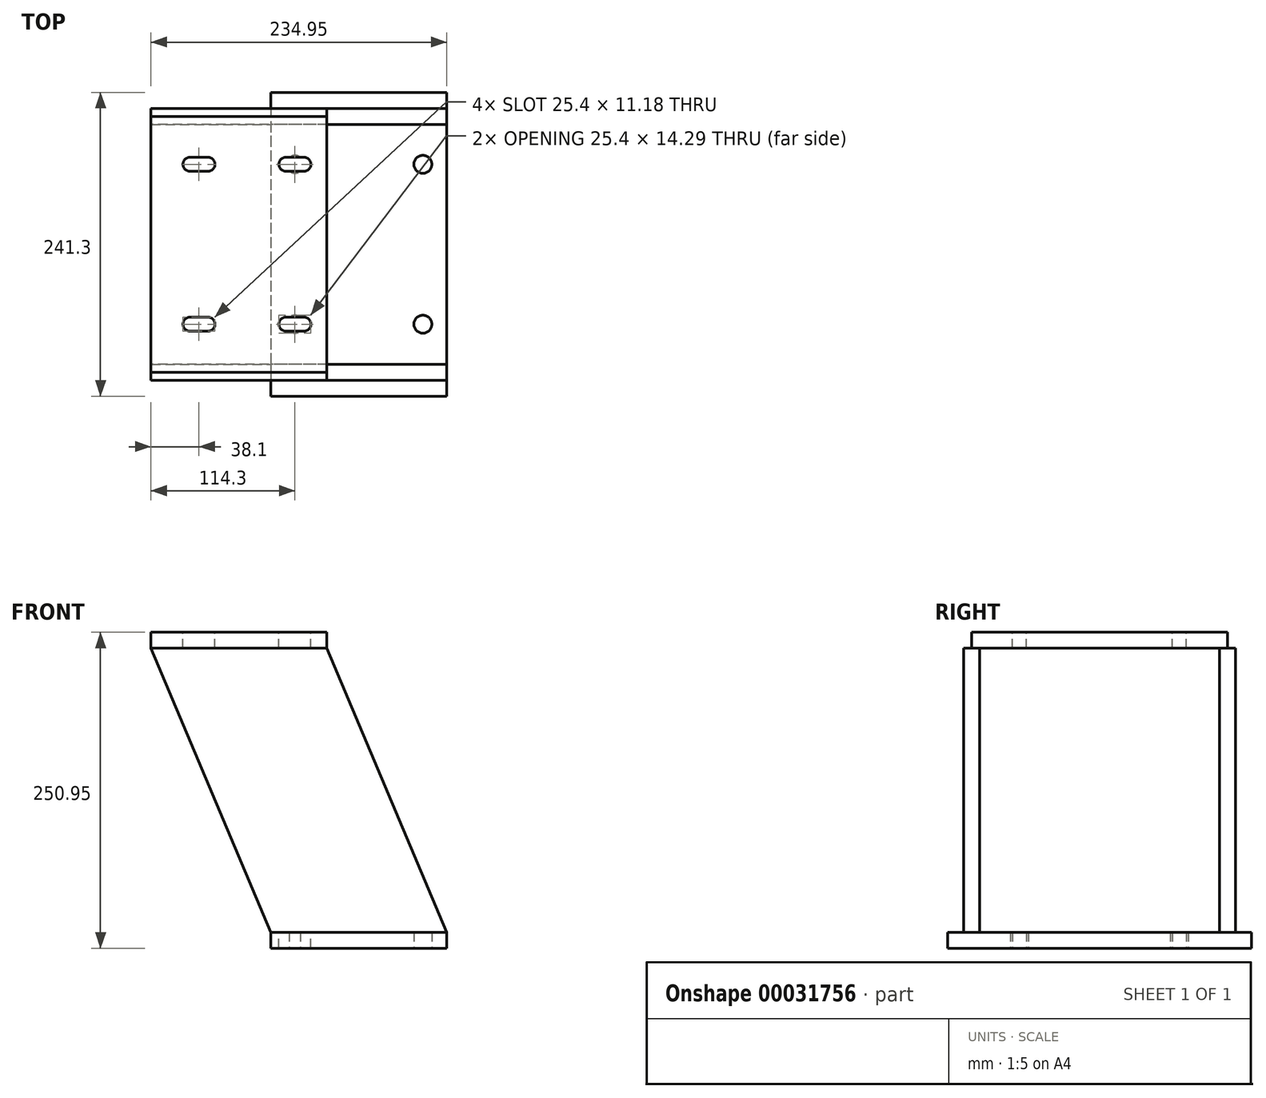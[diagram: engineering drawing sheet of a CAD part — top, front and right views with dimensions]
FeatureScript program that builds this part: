
annotation { "Feature Type Name" : "Feature", "Feature Type Description" : "" }
export const myFeature = defineFeature(function(context is Context, id is Id, definition is map)
    precondition{}
    {
        {
            var Q0;
            Q0=qCreatedBy(makeId("Top.planeOp"),FACE);
            var sketch = newSketch(context, id + "F0", { "sketchPlane" : qUnion([Q0])});
            skLineSegment(sketch, "E0.rect.bottom", {"start": v(-69.85, 120.65) * mm, "end": v(69.85, 120.65) * mm});
            skLineSegment(sketch, "E0.rect.top", {"start": v(-69.85, -120.65) * mm, "end": v(69.85, -120.65) * mm});
            skLineSegment(sketch, "E0.rect.left", {"start": v(-69.85, 120.65) * mm, "end": v(-69.85, -120.65) * mm});
            skLineSegment(sketch, "E0.rect.right", {"start": v(69.85, 120.65) * mm, "end": v(69.85, -120.65) * mm});
            skPoint(sketch, "E0.rect.middle", {"position": v(0, 0) * mm});
            skLineSegment(sketch, "E1.0", {"start": v(50.8, 120.65) * mm, "end": v(50.8, -120.65) * mm, "construction": true});
            skLineSegment(sketch, "E2.0", {"start": v(-50.8, 120.65) * mm, "end": v(-50.8, -120.65) * mm, "construction": true});
            skLineSegment(sketch, "E3", {"start": v(-106.44, 0) * mm, "end": v(168.4, 0) * mm, "construction": true});
            skLineSegment(sketch, "E4.0", {"start": v(-106.44, 63.5) * mm, "end": v(168.4, 63.5) * mm, "construction": true});
            skCircle(sketch, "E5", {"center": v(-50.8, 63.5) * mm, "radius": 7.14 * mm});
            skCircle(sketch, "E6", {"center": v(50.8, 63.5) * mm, "radius": 7.14 * mm});
            skCircle(sketch, "E7.MirrorC", {"center": v(-50.8, -63.5) * mm, "radius": 7.14 * mm});
            skCircle(sketch, "E8.MirrorC", {"center": v(50.8, -63.5) * mm, "radius": 7.14 * mm});
            skSolve(sketch);
        }
        {
            var Q0;
            Q0 = qSketchRegion(id + "F0", true);
            extrude(context, id + "F1", {"entities" : qUnion([Q0]), "depth" : 12.7 * mm});
        }
        {
            var Q0;
            Q0=makeQuery(id+"F1.opExtrude","CAP_FACE",FACE,{"disambiguationData":[OSD([sQuery(id+"F0.wireOp",EDGE,"E0.rect.bottom"),sQuery(id+"F0.wireOp",EDGE,"E0.rect.top"),sQuery(id+"F0.wireOp",EDGE,"E0.rect.left"),sQuery(id+"F0.wireOp",EDGE,"E0.rect.right"),sQuery(id+"F0.wireOp",EDGE,"E5"),sQuery(id+"F0.wireOp",EDGE,"E6"),sQuery(id+"F0.wireOp",EDGE,"E7.MirrorC"),sQuery(id+"F0.wireOp",EDGE,"E8.MirrorC")])],"isStart":false});
            var sketch = newSketch(context, id + "F2", { "sketchPlane" : qUnion([Q0])});
            skLineSegment(sketch, "E9.bottom", {"start": v(69.85, -95.25) * mm, "end": v(-165.1, -95.25) * mm});
            skLineSegment(sketch, "E9.top", {"start": v(69.85, -107.95) * mm, "end": v(-165.1, -107.95) * mm});
            skLineSegment(sketch, "E9.left", {"start": v(69.85, -95.25) * mm, "end": v(69.85, -107.95) * mm});
            skLineSegment(sketch, "E9.right", {"start": v(-165.1, -95.25) * mm, "end": v(-165.1, -107.95) * mm});
            skLineSegment(sketch, "E10", {"start": v(-155.1, 0) * mm, "end": v(166.42, 0) * mm, "construction": true});
            skLineSegment(sketch, "E11.MirrorCS", {"start": v(69.85, 95.25) * mm, "end": v(-165.1, 95.25) * mm});
            skLineSegment(sketch, "E12.MirrorCS", {"start": v(69.85, 107.95) * mm, "end": v(-165.1, 107.95) * mm});
            skLineSegment(sketch, "E13.MirrorCS", {"start": v(-165.1, 95.25) * mm, "end": v(-165.1, 107.95) * mm});
            skLineSegment(sketch, "E14.MirrorCS", {"start": v(69.85, 95.25) * mm, "end": v(69.85, 107.95) * mm});
            skLineSegment(sketch, "E15.MirrorCS", {"start": v(69.85, -107.95) * mm, "end": v(-165.1, -107.95) * mm, "construction": true});
            skLineSegment(sketch, "E16.MirrorCS", {"start": v(69.85, -95.25) * mm, "end": v(-165.1, -95.25) * mm, "construction": true});
            skLineSegment(sketch, "E17.MirrorCS", {"start": v(-165.1, -95.25) * mm, "end": v(-165.1, -107.95) * mm, "construction": true});
            skLineSegment(sketch, "E18.MirrorCS", {"start": v(69.85, -95.25) * mm, "end": v(69.85, -107.95) * mm, "construction": true});
            skSolve(sketch);
        }
        {
            var Q0;
            Q0 = qSketchRegion(id + "F2", true);
            extrude(context, id + "F3", {"entities" : qUnion([Q0]), "depth" : 225.55 * mm});
        }
        {
            var Q0;
            Q0=qCreatedBy(makeId("Front.planeOp"),FACE);
            var sketch = newSketch(context, id + "F4", { "sketchPlane" : qUnion([Q0])});
            skLineSegment(sketch, "E19.0", {"start": v(69.85, 238.25) * mm, "end": v(-165.1, 238.25) * mm, "construction": true});
            skLineSegment(sketch, "E20.bottom", {"start": v(-165.1, 238.25) * mm, "end": v(-25.4, 238.25) * mm});
            skLineSegment(sketch, "E20.top", {"start": v(-165.1, 250.95) * mm, "end": v(-25.4, 250.95) * mm});
            skLineSegment(sketch, "E20.left", {"start": v(-165.1, 238.25) * mm, "end": v(-165.1, 250.95) * mm});
            skLineSegment(sketch, "E20.right", {"start": v(-25.4, 238.25) * mm, "end": v(-25.4, 250.95) * mm});
            skSolve(sketch);
        }
        {
            var Q0;
            Q0 = qSketchRegion(id + "F4", true);
            extrude(context, id + "F5", {"entities" : qUnion([Q0]), "endBound" : BoundingType.SYMMETRIC, "depth" : 203.2 * mm});
        }
        {
            var Q0;
            Q0=makeQuery(id+"F3.opExtrude","SWEPT_FACE",FACE,{"disambiguationData":[OSD([sQuery(id+"F2.wireOp",EDGE,"E9.top")])]});
            var sketch = newSketch(context, id + "F6", { "sketchPlane" : qUnion([Q0])});
            skLineSegment(sketch, "E21.0", {"start": v(-69.85, 12.7) * mm, "end": v(-69.85, 0) * mm, "construction": true});
            skLineSegment(sketch, "E22.0", {"start": v(-165.1, 238.25) * mm, "end": v(-165.1, 12.7) * mm, "construction": true});
            skLineSegment(sketch, "E23.0", {"start": v(-25.4, 238.25) * mm, "end": v(-25.4, 250.95) * mm, "construction": true});
            skLineSegment(sketch, "E24.0", {"start": v(69.85, 238.25) * mm, "end": v(69.85, 12.7) * mm, "construction": true});
            skLineSegment(sketch, "E25", {"start": v(-165.1, 238.25) * mm, "end": v(-69.85, 12.7) * mm});
            skLineSegment(sketch, "E26", {"start": v(-25.4, 238.25) * mm, "end": v(69.85, 12.7) * mm});
            skLineSegment(sketch, "E27.0.0", {"start": v(-165.1, 12.7) * mm, "end": v(-69.85, 12.7) * mm});
            skLineSegment(sketch, "E27.0.1", {"start": v(69.85, 12.7) * mm, "end": v(69.85, 238.25) * mm});
            skLineSegment(sketch, "E27.0.2", {"start": v(69.85, 238.25) * mm, "end": v(-25.4, 238.25) * mm});
            skLineSegment(sketch, "E27.0.3", {"start": v(-165.1, 238.25) * mm, "end": v(-165.1, 12.7) * mm});
            skSolve(sketch);
        }
        {
            var Q0;
            Q0 = qSketchRegion(id + "F6", true);
            var Q1;
            Q1=makeQuery(id+"F3.opExtrude","SWEPT_FACE",FACE,{"disambiguationData":[OSD([sQuery(id+"F2.wireOp",EDGE,"E12.MirrorCS")])]});
            extrude(context, id + "F7", {"entities" : qUnion([Q0, Q1]), "operationType" : NewBodyOperationType.REMOVE, "endBound" : BoundingType.THROUGH_ALL, "oppositeDirection" : true, "depth" : 25.4 * mm});
        }
        {
            var Q0;
            Q0=makeQuery(id+"F5.opExtrude","SWEPT_FACE",FACE,{"disambiguationData":[OSD([sQuery(id+"F4.wireOp",EDGE,"E20.top")])]});
            var sketch = newSketch(context, id + "F8", { "sketchPlane" : qUnion([Q0])});
            skLineSegment(sketch, "E28", {"start": v(-165.1, 0) * mm, "end": v(-25.4, 0) * mm, "construction": true});
            skLineSegment(sketch, "E29.0", {"start": v(-88.9, -101.6) * mm, "end": v(-88.9, 101.6) * mm, "construction": true});
            skLineSegment(sketch, "E30.0", {"start": v(-50.8, -101.6) * mm, "end": v(-50.8, 101.6) * mm, "construction": true});
            skLineSegment(sketch, "E31.0", {"start": v(-165.1, 63.5) * mm, "end": v(-25.4, 63.5) * mm, "construction": true});
            skLineSegment(sketch, "E32.0", {"start": v(-43.69, -101.6) * mm, "end": v(-43.69, 101.6) * mm, "construction": true});
            skLineSegment(sketch, "E33.0", {"start": v(-57.91, -101.6) * mm, "end": v(-57.91, 101.6) * mm, "construction": true});
            skLineSegment(sketch, "E34", {"start": v(-57.91, 63.5) * mm, "end": v(-43.69, 63.5) * mm});
            skArc(sketch, "E35.0.startCap", {"start": v(-57.91, 57.91) * mm, "mid": v(-63.5, 63.5) * mm, "end": v(-57.91, 69.09) * mm});
            skArc(sketch, "E35.0.endCap", {"start": v(-43.69, 69.09) * mm, "mid": v(-38.1, 63.5) * mm, "end": v(-43.69, 57.91) * mm});
            skLineSegment(sketch, "E35.0.left", {"start": v(-57.91, 69.09) * mm, "end": v(-43.69, 69.09) * mm});
            skLineSegment(sketch, "E35.0.right", {"start": v(-57.91, 57.91) * mm, "end": v(-43.69, 57.91) * mm});
            skLineSegment(sketch, "E36.0.1.0", {"start": v(-57.91, -63.5) * mm, "end": v(-43.69, -63.5) * mm});
            skArc(sketch, "E36.0.1.1", {"start": v(-57.91, -69.09) * mm, "mid": v(-63.5, -63.5) * mm, "end": v(-57.91, -57.91) * mm});
            skArc(sketch, "E36.0.1.2", {"start": v(-43.69, -57.91) * mm, "mid": v(-38.1, -63.5) * mm, "end": v(-43.69, -69.09) * mm});
            skLineSegment(sketch, "E36.0.1.3", {"start": v(-57.91, -57.91) * mm, "end": v(-43.69, -57.91) * mm});
            skLineSegment(sketch, "E36.0.1.4", {"start": v(-57.91, -69.09) * mm, "end": v(-43.69, -69.09) * mm});
            skLineSegment(sketch, "E36.1.0.0", {"start": v(-134.11, 63.5) * mm, "end": v(-119.89, 63.5) * mm});
            skArc(sketch, "E36.1.0.1", {"start": v(-134.11, 57.91) * mm, "mid": v(-139.7, 63.5) * mm, "end": v(-134.11, 69.09) * mm});
            skArc(sketch, "E36.1.0.2", {"start": v(-119.89, 69.09) * mm, "mid": v(-114.3, 63.5) * mm, "end": v(-119.89, 57.91) * mm});
            skLineSegment(sketch, "E36.1.0.3", {"start": v(-134.11, 69.09) * mm, "end": v(-119.89, 69.09) * mm});
            skLineSegment(sketch, "E36.1.0.4", {"start": v(-134.11, 57.91) * mm, "end": v(-119.89, 57.91) * mm});
            skLineSegment(sketch, "E36.1.1.0", {"start": v(-134.11, -63.5) * mm, "end": v(-119.89, -63.5) * mm});
            skArc(sketch, "E36.1.1.1", {"start": v(-134.11, -69.09) * mm, "mid": v(-139.7, -63.5) * mm, "end": v(-134.11, -57.91) * mm});
            skArc(sketch, "E36.1.1.2", {"start": v(-119.89, -57.91) * mm, "mid": v(-114.3, -63.5) * mm, "end": v(-119.89, -69.09) * mm});
            skLineSegment(sketch, "E36.1.1.3", {"start": v(-134.11, -57.91) * mm, "end": v(-119.89, -57.91) * mm});
            skLineSegment(sketch, "E36.1.1.4", {"start": v(-134.11, -69.09) * mm, "end": v(-119.89, -69.09) * mm});
            skLineSegment(sketch, "E36.direction1", {"start": v(-57.91, 63.5) * mm, "end": v(-134.11, 63.5) * mm, "construction": true});
            skLineSegment(sketch, "E36.direction2", {"start": v(-57.91, 63.5) * mm, "end": v(-57.91, -63.5) * mm, "construction": true});
            skSolve(sketch);
        }
        {
            var Q0;
            Q0 = qSketchRegion(id + "F8", true);
            extrude(context, id + "F9", {"entities" : qUnion([Q0]), "operationType" : NewBodyOperationType.REMOVE, "endBound" : BoundingType.THROUGH_ALL, "oppositeDirection" : true, "depth" : 25.4 * mm});
        }
    });
